# Revit family: LLIFE-PRO-xx-SM-WP_V1.0_Non-Hosted_R19
name_source: partatom
category: Lighting Fixtures
units: mm (PartAtom-declared; Revit-internal decimal feet)

## family parameters
Always vertical = Yes
Cut with Voids When Loaded = No
Light Source = Yes
OmniClass Number = 23.80.70.00
OmniClass Title = Lighting
Part Type = Normal
Room Calculation Point = No
Round Connector Dimension = Use Diameter
Shared = No
Work Plane-Based = No

## types (4) — shared parameters
AS2293 Classification = C0=D80 C90=D80
Battery = 3.3V 5000mAh
Battery Type = Lithium Nanophosphate
Charging Method = Intelligent Current Limited Constant Voltage
Color Filter = 16777215
Construction = Polycarbonate Enclosure
Dimensions (L x W x H) = 247mm x 129mm x 51mm
Dimming Lamp Color Temperature Shift = <None>
Emergency Lumen Output = 410.7
Emit Shape Visible in Rendering = No
Emit from Rectangle Length = 1219 mm
Emit from Rectangle Width = 610 mm
IK Rating = IK08
IP Rating = IP65
Lamp = Dual LED (Lifetime warranty on the lamp head and loom assembly)
Manufacturer = Clevertronics
Mounting = Surface Mounted
Operating Mode = Non-maintained
Operating Temperature = 0˚C to 40˚C
Operating Voltage = 240V AC; 50Hz
Photometric Web File = 200240PH_LLIFEM-PRO-SM-WP-HV(AS2293,2-hr_Photometry).IES
Product Description = Economy Lithium Lifelight, Weatherproof, Surface Mounted Emergency Light
Replacement Battery = 1530231 BATTERY:L10 3.3V 5AH. 200mm lead.no Brkt
8050170
LED:
Replacement Emergency Driver = 8002924 PCA: xLIFEPro SM #CT10142-L9 2C250/550 CTP AU
Replacement Emergency Lamp = 8050170 LED: HWSUB: CT10668-D1
Tilt Angle = 90.00°
Weight = 0.8kg

## per-type parameters (varying)
| type | Description | MIC Number | Power Consumption | Power Consumption (Standby) | Testing Node | Testing System | Type Comments |
| LLIFE-PRO-SM-WP | Lifelight Pro, WProof Surface Mount, LP, CTP, OWC | AUT01320130001 | 2.7W | 0.4W |  | Clevertest Plus Enabled (Not activated by default) | L10 Optimum Lifelight PRO, High Performance, Weatherproof, Surface Mounted Emergency Light, Enabled with Clevertest Plus |
| LLIFE-PRO-SM-WP-HV | Lifelight Pro, Weatherproof Surface Mount, L10, HV | AUT01820070001 | 3W | 0.7W | 8003191 PCA: RF Node CT10678-A9 Int Antenna LLPro | Zoneworks XT Hive (RF) | L10 Optimum Lifelight PRO, High Performance, Weatherproof, Surface Mounted Emergency Light |
| LLIFE-PRO-SM-WP-DALI | Lifelight Pro,Weatherproof SurfaceMnt,L10,Dali Reg | AUT01220240002 | 3W | 0.7W | 8003060 PCA: New DALI #CT10629-Ax | DALI registered | L10 Optimum Lifelight PRO, High Performance, Weatherproof, Surface Mounted Emergency Light |
| LLIFE-PRO-SM-WP-ZW | Lifelight Pro, Weatherproof Surface Mount, L10, ZW | AUT01120100001 | 3W | 0.7W | 8001450 PCA:Powerline Node ZW, #CT10310-A6 | Zoneworks computerised testing | L10 Optimum Lifelight PRO, High Performance, Weatherproof, Surface Mounted Emergency Light |

note: column(s) folded — value = type name in every type: Model

## geometry (parser evidence)
native form markers: Sweep x2
no freeform markers — native parametric forms only
